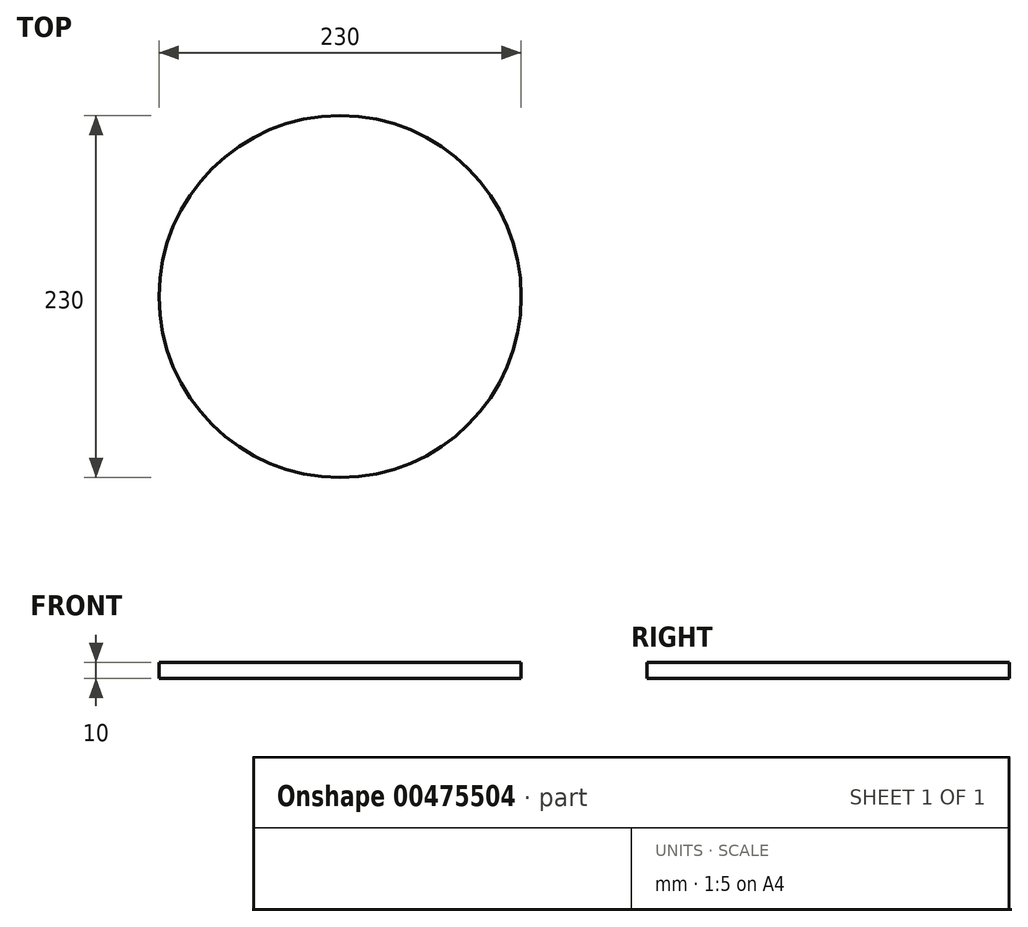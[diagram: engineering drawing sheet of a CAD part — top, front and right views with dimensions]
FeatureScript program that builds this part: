
annotation { "Feature Type Name" : "Feature", "Feature Type Description" : "" }
export const myFeature = defineFeature(function(context is Context, id is Id, definition is map)
    precondition{}
    {
        {
            var Q0;
            Q0=qCreatedBy(makeId("Top.planeOp"),FACE);
            var sketch = newSketch(context, id + "F0", { "sketchPlane" : qUnion([Q0])});
            skArc(sketch, "E0", {"start": v(0, 115) * mm, "mid": v(-81.32, -81.32) * mm, "end": v(115, 0) * mm});
            skLineSegment(sketch, "E1", {"start": v(0, 0) * mm, "end": v(0, 121.43) * mm, "construction": true});
            skLineSegment(sketch, "E2", {"start": v(0, 121.43) * mm, "end": v(0, 0) * mm, "construction": true});
            skLineSegment(sketch, "E3", {"start": v(0, 0) * mm, "end": v(184.44, 0) * mm, "construction": true});
            skLineSegment(sketch, "E4", {"start": v(0, 0) * mm, "end": v(-104.12, 104.12) * mm, "construction": true});
            skLineSegment(sketch, "E5", {"start": v(0, 0) * mm, "end": v(116.24, -116.24) * mm, "construction": true});
            skLineSegment(sketch, "E6", {"start": v(-50.96, 130.5) * mm, "end": v(40.02, -119.47) * mm, "construction": true});
            skLineSegment(sketch, "E7", {"start": v(0, 0) * mm, "end": v(167, -60.78) * mm, "construction": true});
            skLineSegment(sketch, "E8", {"start": v(0, 0) * mm, "end": v(-94.52, 44.08) * mm, "construction": true});
            skCircle(sketch, "E9", {"center": v(0, 0) * mm, "radius": 115 * mm});
            skLineSegment(sketch, "E10", {"start": v(-27.98, 67.37) * mm, "end": v(-27.46, 65.94) * mm});
            skLineSegment(sketch, "E11", {"start": v(21.87, -69.6) * mm, "end": v(21.35, -68.17) * mm});
            skLineSegment(sketch, "E12", {"start": v(36.18, -36.18) * mm, "end": v(35.1, -35.1) * mm});
            skLineSegment(sketch, "E13", {"start": v(-35.1, 35.1) * mm, "end": v(-36.18, 36.18) * mm});
            skLineSegment(sketch, "E14", {"start": v(-84.48, 39.4) * mm, "end": v(-85.86, 40.04) * mm});
            skLineSegment(sketch, "E15", {"start": v(89.02, -32.4) * mm, "end": v(87.6, -31.88) * mm});
            skSolve(sketch);
        }
        {
            var Q0;
            Q0=qSketchRegion(id+"F0",true);
            extrude(context, id + "F1", {"entities" : qUnion([Q0]), "depth" : 10 * mm, "offsetDistance" : 25 * mm});
        }
    });
